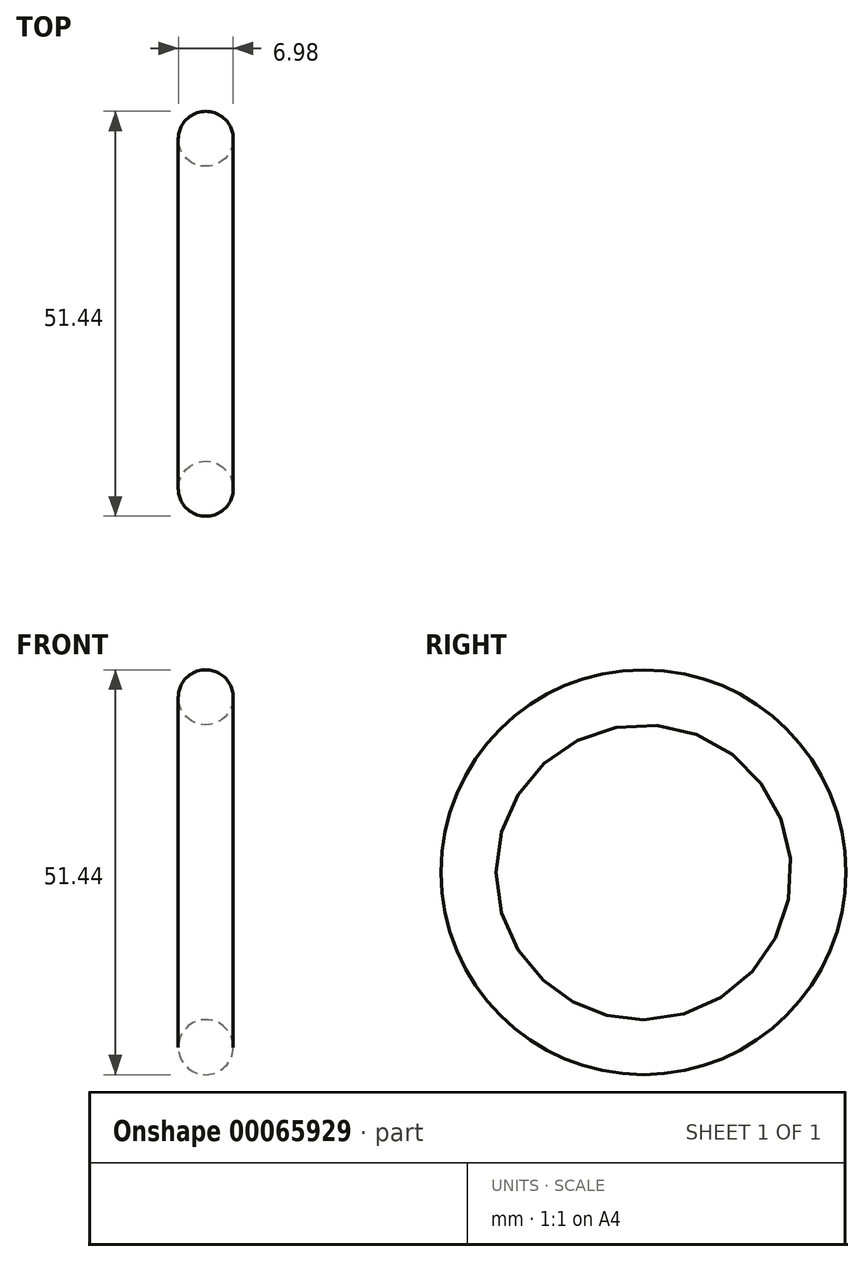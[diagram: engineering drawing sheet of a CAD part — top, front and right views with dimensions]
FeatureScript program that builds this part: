
annotation { "Feature Type Name" : "Feature", "Feature Type Description" : "" }
export const myFeature = defineFeature(function(context is Context, id is Id, definition is map)
    precondition{}
    {
        {
            var Q0;
            Q0=qCreatedBy(makeId("Front.planeOp"),FACE);
            var sketch = newSketch(context, id + "F0", { "sketchPlane" : qUnion([Q0])});
            skLineSegment(sketch, "E0", {"start": v(0, 0) * mm, "end": v(-6.06, 0) * mm, "construction": true});
            skCircle(sketch, "E1", {"center": v(0, 22.23) * mm, "radius": 3.5 * mm});
            skSolve(sketch);
        }
        {
            var Q0;
            Q0=makeQuery(id+"F0.imprint","IMPRINT",FACE,{"disambiguationData":[TD([[makeQuery(id+"F0.imprint","IMPRINT",EDGE,{"derivedFrom":sQuery(id+"F0.wireOp",EDGE,"E1")}),1.0]])]});
            var Q1;
            Q1=sQuery(id+"F0.wireOp",EDGE,"E0");
            revolve(context, id + "F1", {"entities" : qUnion([Q0]), "axis" : qUnion([Q1]), "revolveType" : RevolveType.FULL});
        }
    });
